# Revit family: BAS-IP_Контроллер_EVRC-IP
name_source: partatom
category: Устройства связи
units: mm (PartAtom-declared; Revit-internal decimal feet)

## family parameters
Всегда вертикально = Да
На основе рабочей плоскости = Нет
Общий = Нет
При загрузке вырезать с полостями = Нет
Размер круглого соединителя = Использовать диаметр
Сохранять ориентацию аннотаций = Нет
Тип детали = Нормальный
Точка расчета площади = Нет

## types (1)
- EVRC-IP
    ADSK_Единица измерения = шт.
    ADSK_Завод-изготовитель = BAS-IP
    ADSK_Количество = 1
    ADSK_Марка = EVRC-IP
    ADSK_Материал = Black silver
    ADSK_Наименование = Контроллер лифта
    Габаритные размеры = 196 × 90 × 38 мм
    Изготовитель = BAS-IP
    Класс степени защиты = IP30
    Максимальное количество модулей в одной системе = 98
    Относительная влажность хранения = 20% - 93%
    Потребляемая мощность в работе = 7 Вт
    Потребляемая мощность в режиме ожидания = 1 Вт
    Потребляемое напряжение = POE support
    Температурный режим = -40 – +75 °С
